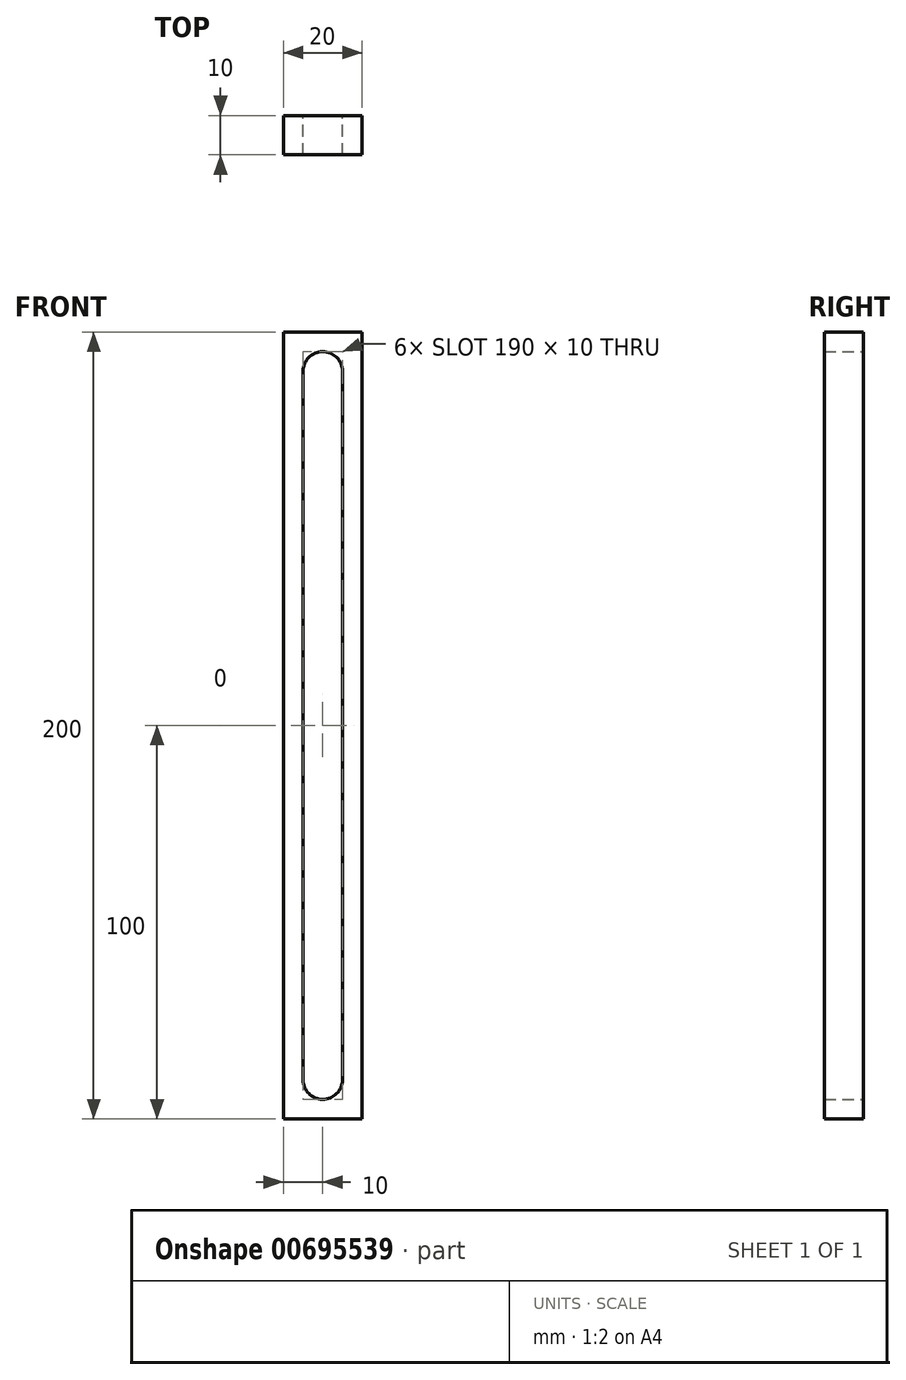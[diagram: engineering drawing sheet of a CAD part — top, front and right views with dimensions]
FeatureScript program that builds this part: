
annotation { "Feature Type Name" : "Feature", "Feature Type Description" : "" }
export const myFeature = defineFeature(function(context is Context, id is Id, definition is map)
    precondition{}
    {
        {
            var Q0;
            Q0=qCreatedBy(makeId("Front.planeOp"),FACE);
            var sketch = newSketch(context, id + "F0", { "sketchPlane" : qUnion([Q0])});
            skLineSegment(sketch, "E0.bottom", {"start": v(10, -100) * mm, "end": v(-10, -100) * mm});
            skLineSegment(sketch, "E0.top", {"start": v(10, 100) * mm, "end": v(-10, 100) * mm});
            skLineSegment(sketch, "E0.left", {"start": v(10, -100) * mm, "end": v(10, 100) * mm});
            skLineSegment(sketch, "E0.right", {"start": v(-10, -100) * mm, "end": v(-10, 100) * mm});
            skPoint(sketch, "E0.middle", {"position": v(0, 0) * mm});
            skLineSegment(sketch, "E1.bottom", {"start": v(0, -95) * mm, "end": v(0, -95) * mm});
            skLineSegment(sketch, "E1.top", {"start": v(0, 95) * mm, "end": v(0, 95) * mm});
            skLineSegment(sketch, "E1.left", {"start": v(5, -90) * mm, "end": v(5, 90) * mm});
            skLineSegment(sketch, "E1.right", {"start": v(-5, -90) * mm, "end": v(-5, 90) * mm});
            skPoint(sketch, "E2.visualSharp", {"position": v(-5, 95) * mm});
            skArc(sketch, "E2.filletArc", {"start": v(0, 95) * mm, "mid": v(-3.54, 93.54) * mm, "end": v(-5, 90) * mm});
            skPoint(sketch, "E3.visualSharp", {"position": v(5, 95) * mm});
            skArc(sketch, "E3.filletArc", {"start": v(5, 90) * mm, "mid": v(3.54, 93.54) * mm, "end": v(0, 95) * mm});
            skPoint(sketch, "E4.visualSharp", {"position": v(5, -95) * mm});
            skArc(sketch, "E4.filletArc", {"start": v(0, -95) * mm, "mid": v(3.54, -93.54) * mm, "end": v(5, -90) * mm});
            skPoint(sketch, "E5.visualSharp", {"position": v(-5, -95) * mm});
            skArc(sketch, "E5.filletArc", {"start": v(-5, -90) * mm, "mid": v(-3.54, -93.54) * mm, "end": v(0, -95) * mm});
            skSolve(sketch);
        }
        {
            var Q0;
            Q0=makeQuery(id+"F0.imprint","IMPRINT",FACE,{"disambiguationData":[TD([[makeQuery(id+"F0.imprint","IMPRINT",EDGE,{"derivedFrom":sQuery(id+"F0.wireOp",EDGE,"E0.bottom")}),-1.0]])]});
            extrude(context, id + "F1", {"entities" : qUnion([Q0]), "depth" : 10 * mm, "offsetDistance" : 25 * mm});
        }
    });
